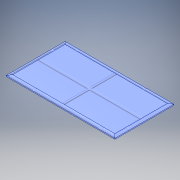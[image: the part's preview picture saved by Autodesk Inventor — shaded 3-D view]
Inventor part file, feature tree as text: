
AUTODESK INVENTOR PART (.ipt)
format: ipt  version: 2019 (Build 230136000, 136)  size: 110,080 bytes
history: native  units: mm
features: chamfer x4, extrude x1, sketch x1
ambient origin geometry x8: Origin, YZ Plane, XZ Plane, XY Plane, X Axis, Y Axis, Z Axis, Center Point
bodies: Solid1 (feature_tree)
feature tree (6):
  extrude  "Extrusion1"  Depth=90.0mm
  chamfer  "Chamfer1"  Distance=2.54mm
  chamfer  "Chamfer2"  Distance=5.0mm Angle=45.0deg
  chamfer  "Chamfer3"  Distance=5.0mm Angle=45.0deg
  chamfer  "Chamfer4"  Distance=5.0mm Angle=45.0deg
  sketch  "Sketch1"  dims[d0=166.0mm d1=90.0mm d2=2.54mm d3=0.0mm d4=5.0mm d5=1.0mm d6=45.0deg d7=5.0mm d8=1.0mm d9=45.0deg d10=5.0mm d11=1.0mm d12=45.0deg d13=5.0mm d14=1.0mm d15=45.0deg]
